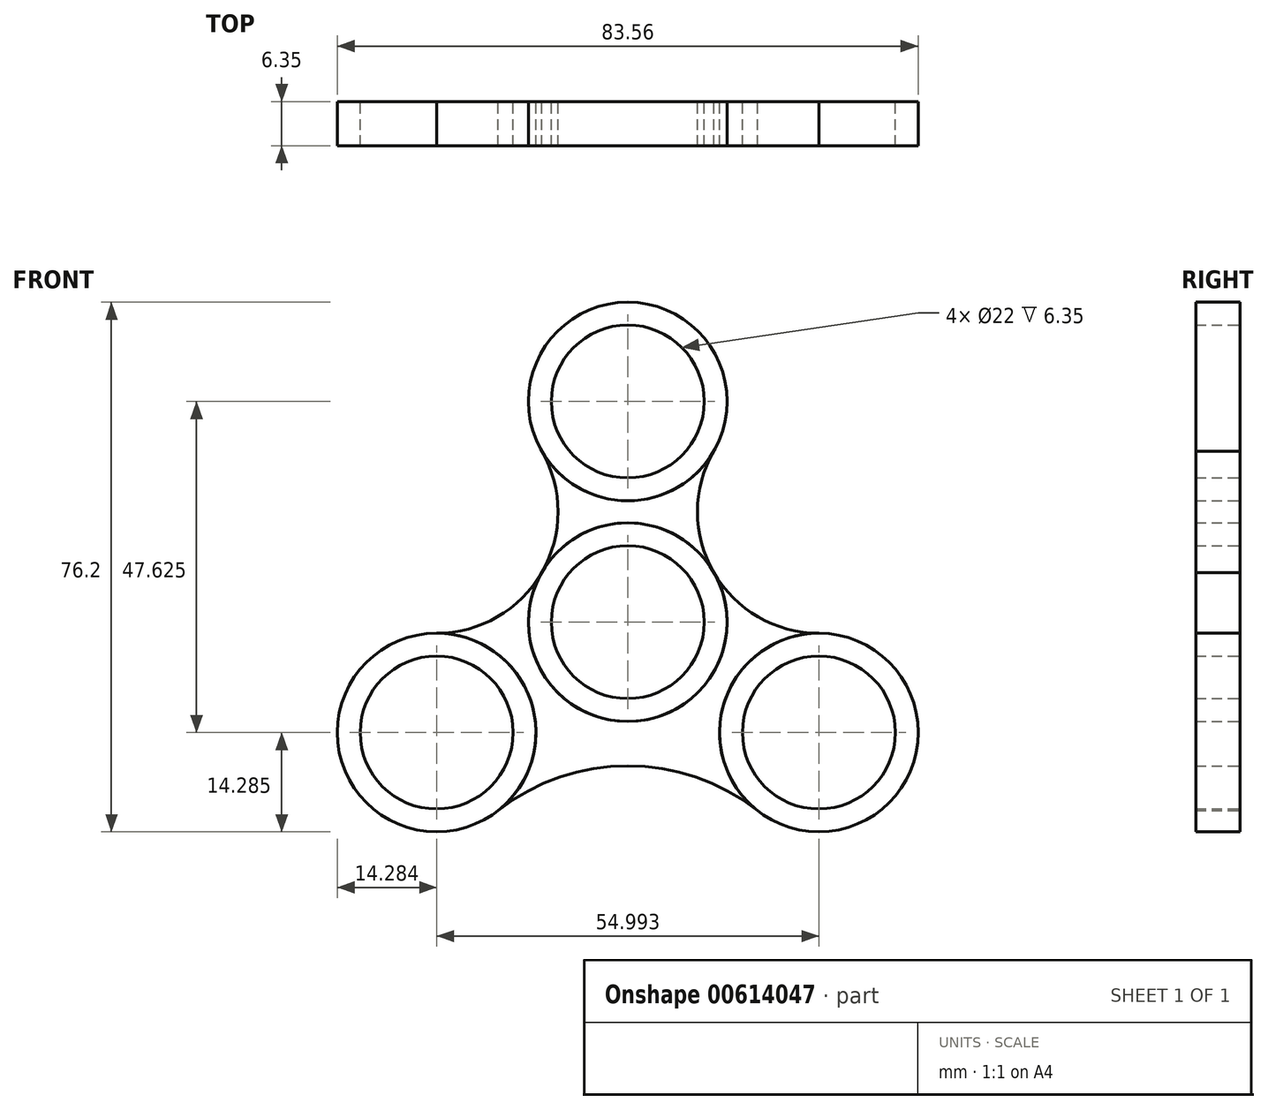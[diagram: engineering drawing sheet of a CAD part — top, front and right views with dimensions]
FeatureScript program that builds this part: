
annotation { "Feature Type Name" : "Feature", "Feature Type Description" : "" }
export const myFeature = defineFeature(function(context is Context, id is Id, definition is map)
    precondition{}
    {
        {
            var Q0;
            Q0=qCreatedBy(makeId("Front.planeOp"),FACE);
            var sketch = newSketch(context, id + "F0", { "sketchPlane" : qUnion([Q0])});
            skCircle(sketch, "E0", {"center": v(0, 0) * mm, "radius": 14.29 * mm});
            skCircle(sketch, "E1", {"center": v(0, 0) * mm, "radius": 11 * mm});
            skCircle(sketch, "E2", {"center": v(0, 31.75) * mm, "radius": 14.29 * mm});
            skCircle(sketch, "E3", {"center": v(0, 31.75) * mm, "radius": 11 * mm});
            skCircle(sketch, "E4.1.0", {"center": v(-27.5, -15.87) * mm, "radius": 11 * mm});
            skCircle(sketch, "E4.1.1", {"center": v(-27.5, -15.87) * mm, "radius": 14.29 * mm});
            skCircle(sketch, "E4.2.0", {"center": v(27.5, -15.88) * mm, "radius": 11 * mm});
            skCircle(sketch, "E4.2.1", {"center": v(27.5, -15.88) * mm, "radius": 14.29 * mm});
            skSolve(sketch);
        }
        {
            var Q0;
            Q0=qCreatedBy(makeId("Front.planeOp"),FACE);
            var sketch = newSketch(context, id + "F1", { "sketchPlane" : qUnion([Q0])});
            skArc(sketch, "E5", {"start": v(-29.02, -1.52) * mm, "mid": v(-11.8, 8.2) * mm, "end": v(-14.7, 27.76) * mm});
            skArc(sketch, "E6", {"start": v(14.7, 27.76) * mm, "mid": v(11.99, 7.85) * mm, "end": v(29.82, -1.43) * mm});
            skArc(sketch, "E7", {"start": v(19.45, -27.75) * mm, "mid": v(0.5, -20.66) * mm, "end": v(-18.7, -27.13) * mm});
            skCircle(sketch, "E8.0", {"center": v(0, 31.75) * mm, "radius": 11 * mm});
            skCircle(sketch, "E9.0", {"center": v(0, 31.75) * mm, "radius": 14.29 * mm});
            skCircle(sketch, "E10.0", {"center": v(27.5, -15.88) * mm, "radius": 11 * mm});
            skCircle(sketch, "E11.0", {"center": v(27.5, -15.88) * mm, "radius": 14.29 * mm});
            skCircle(sketch, "E12.0.0", {"center": v(-27.5, -15.87) * mm, "radius": 11 * mm});
            skCircle(sketch, "E13.0.0", {"center": v(-27.5, -15.87) * mm, "radius": 14.29 * mm});
            skCircle(sketch, "E14.0", {"center": v(0, 0) * mm, "radius": 11 * mm});
            skCircle(sketch, "E15.0", {"center": v(0, 0) * mm, "radius": 14.29 * mm});
            skSolve(sketch);
        }
        {
            var Q0;
            {var subQ0=sQuery(id+"F1.wireOp",EDGE,"E9.0");var subQ1=sQuery(id+"F1.wireOp",EDGE,"E5");var subQ2=makeQuery(id+"F1.imprint","INTERSECT",VERTEX,{"derivedFrom":[subQ1,subQ0]});Q0=makeQuery(id+"F1.imprint","IMPRINT",FACE,{"disambiguationData":[TD([[makeQuery(id+"F1.imprint","IMPRINT",EDGE,{"disambiguationData":[TD([[subQ2,1.0]])],"derivedFrom":subQ1}),-1.0]])]});}
            var Q1;
            Q1=makeQuery(id+"F0.imprint","IMPRINT",FACE,{"disambiguationData":[TD([[makeQuery(id+"F0.imprint","IMPRINT",EDGE,{"derivedFrom":sQuery(id+"F0.wireOp",EDGE,"E2")}),1.0]])]});
            var Q2;
            {var subQ5=sQuery(id+"F1.wireOp",EDGE,"E13.0.0");var subQ9=sQuery(id+"F1.wireOp",EDGE,"E5");var subQ10=makeQuery(id+"F1.imprint","INTERSECT",VERTEX,{"derivedFrom":[subQ9,subQ5]});Q2=makeQuery(id+"F1.imprint","IMPRINT",FACE,{"disambiguationData":[TD([[makeQuery(id+"F1.imprint","IMPRINT",EDGE,{"disambiguationData":[TD([[subQ10,-1.0]])],"derivedFrom":subQ9}),-1.0]])]});}
            var Q3;
            Q3=makeQuery(id+"F0.imprint","IMPRINT",FACE,{"disambiguationData":[TD([[makeQuery(id+"F0.imprint","IMPRINT",EDGE,{"derivedFrom":sQuery(id+"F0.wireOp",EDGE,"E4.1.0")}),-1.0]])]});
            var Q4;
            Q4=makeQuery(id+"F0.imprint","IMPRINT",FACE,{"disambiguationData":[TD([[makeQuery(id+"F0.imprint","IMPRINT",EDGE,{"derivedFrom":sQuery(id+"F0.wireOp",EDGE,"E4.2.0")}),-1.0]])]});
            var Q5;
            Q5=makeQuery(id+"F0.imprint","IMPRINT",FACE,{"disambiguationData":[TD([[makeQuery(id+"F0.imprint","IMPRINT",EDGE,{"derivedFrom":sQuery(id+"F0.wireOp",EDGE,"E0")}),1.0]])]});
            extrude(context, id + "F2", {"entities" : qUnion([Q0, Q1, Q2, Q3, Q4, Q5]), "depth" : 6.35 * mm, "offsetDistance" : 25.4 * mm});
        }
    });
